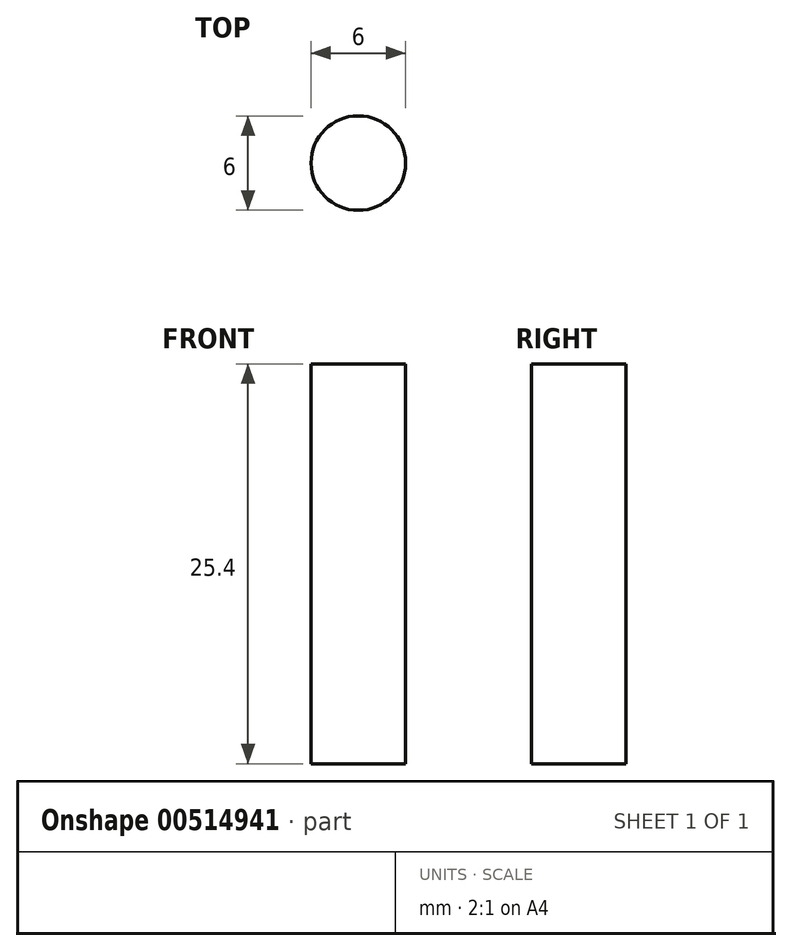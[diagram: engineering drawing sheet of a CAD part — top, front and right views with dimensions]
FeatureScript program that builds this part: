
annotation { "Feature Type Name" : "Feature", "Feature Type Description" : "" }
export const myFeature = defineFeature(function(context is Context, id is Id, definition is map)
    precondition{}
    {
        {
            var Q0;
            Q0=qCreatedBy(makeId("Top.planeOp"),FACE);
            var sketch = newSketch(context, id + "F0", { "sketchPlane" : qUnion([Q0])});
            skCircle(sketch, "E0", {"center": v(0, 0) * mm, "radius": 3 * mm});
            skLineSegment(sketch, "E1", {"start": v(0, 3) * mm, "end": v(0, -3) * mm});
            skSolve(sketch);
        }
        {
            var Q0;
            {var subQ0=sQuery(id+"F0.wireOp",EDGE,"E1");var subQ1=sQuery(id+"F0.wireOp",EDGE,"E0");var subQ2=makeQuery(id+"F0.imprint","INTERSECT",VERTEX,{"disambiguationData":[OD(0.0)],"derivedFrom":[subQ1,subQ0]});Q0=makeQuery(id+"F0.imprint","IMPRINT",FACE,{"disambiguationData":[TD([[makeQuery(id+"F0.imprint","IMPRINT",EDGE,{"disambiguationData":[TD([[subQ2,1.0]])],"derivedFrom":subQ1}),1.0]])]});}
            var Q1;
            {var subQ0=sQuery(id+"F0.wireOp",EDGE,"E1");var subQ1=sQuery(id+"F0.wireOp",EDGE,"E0");var subQ2=makeQuery(id+"F0.imprint","INTERSECT",VERTEX,{"disambiguationData":[OD(0.0)],"derivedFrom":[subQ1,subQ0]});Q1=makeQuery(id+"F0.imprint","IMPRINT",FACE,{"disambiguationData":[TD([[makeQuery(id+"F0.imprint","IMPRINT",EDGE,{"disambiguationData":[TD([[subQ2,-1.0]])],"derivedFrom":subQ1}),1.0]])]});}
            var Q2;
            {var subQ0=sQuery(id+"F0.wireOp",EDGE,"E1");var subQ1=sQuery(id+"F0.wireOp",EDGE,"E0");var subQ2=makeQuery(id+"F0.imprint","INTERSECT",VERTEX,{"disambiguationData":[OD(1.0)],"derivedFrom":[subQ1,subQ0]});Q2=makeQuery(id+"F0.imprint","IMPRINT",FACE,{"disambiguationData":[TD([[makeQuery(id+"F0.imprint","IMPRINT",EDGE,{"disambiguationData":[TD([[subQ2,1.0]])],"derivedFrom":subQ1}),1.0]])]});}
            var Q3;
            {var subQ0=sQuery(id+"F0.wireOp",EDGE,"E1");var subQ1=sQuery(id+"F0.wireOp",EDGE,"E0");var subQ2=makeQuery(id+"F0.imprint","INTERSECT",VERTEX,{"disambiguationData":[OD(1.0)],"derivedFrom":[subQ1,subQ0]});Q3=makeQuery(id+"F0.imprint","IMPRINT",FACE,{"disambiguationData":[TD([[makeQuery(id+"F0.imprint","IMPRINT",EDGE,{"disambiguationData":[TD([[subQ2,-1.0]])],"derivedFrom":subQ1}),1.0]])]});}
            extrude(context, id + "F1", {"entities" : qUnion([Q0, Q1, Q2, Q3]), "depth" : 25.4 * mm, "offsetDistance" : 25.4 * mm});
        }
        {
            var Q0;
            Q0=makeQuery(id+"F1.opExtrude","SWEPT_BODY",BODY,{"disambiguationData":[OSD([sQuery(id+"F0.wireOp",EDGE,"E0")])]});
            transform(context, id + "F2", {"entities" : qUnion([Q0]), "transformType" : TransformType.TRANSLATION_3D, "dx" : 0 * mm, "dy" : 0 * mm, "dz" : -65.02 * mm, "makeCopy" : false});
        }
    });
